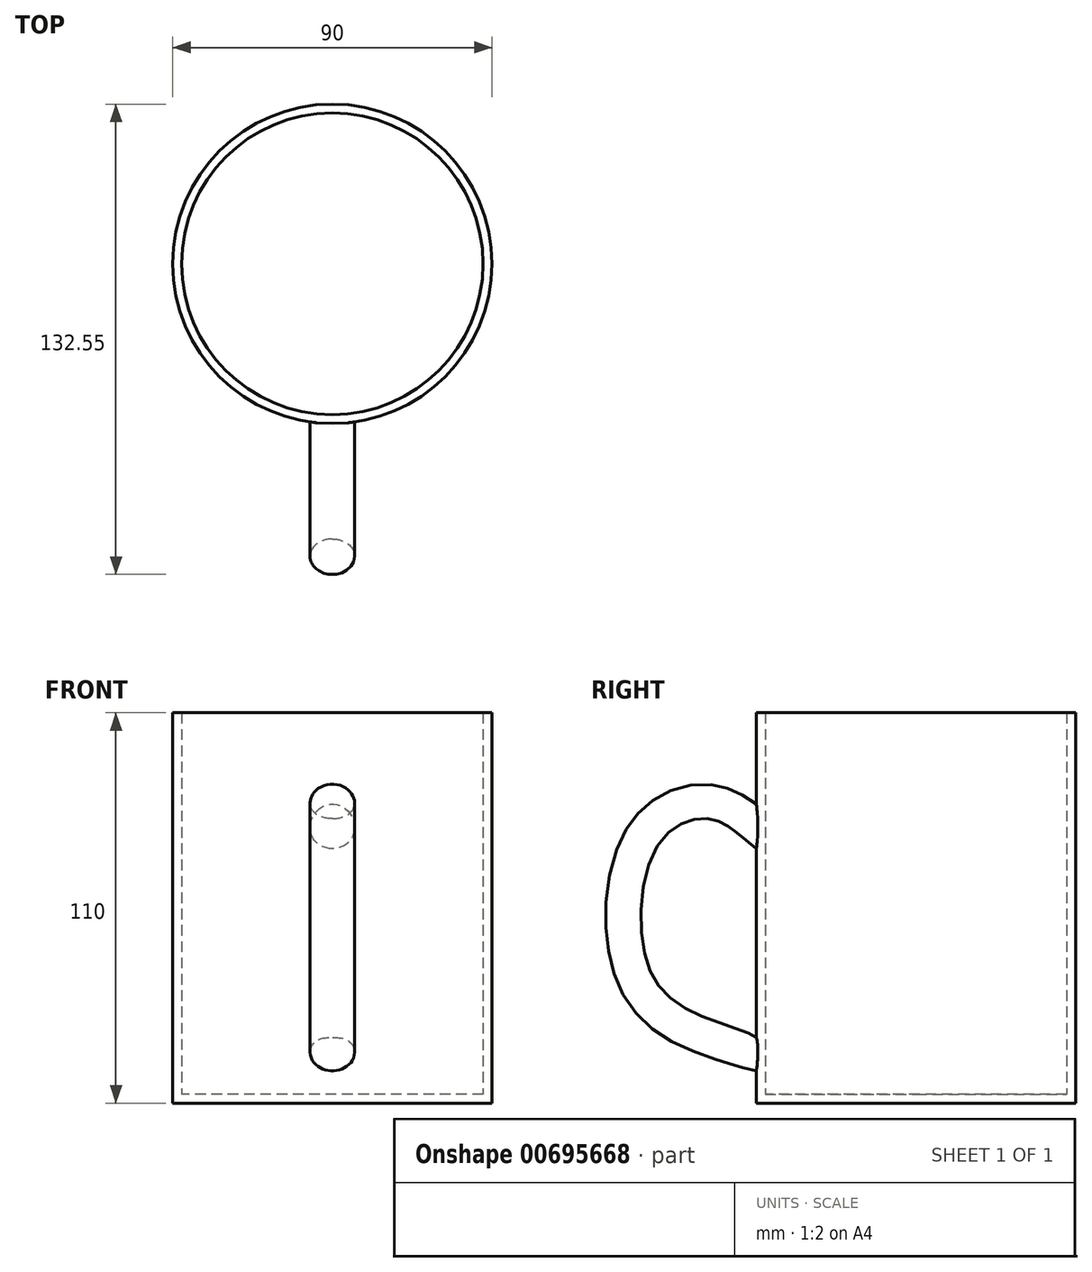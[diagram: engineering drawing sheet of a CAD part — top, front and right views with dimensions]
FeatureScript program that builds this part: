
annotation { "Feature Type Name" : "Feature", "Feature Type Description" : "" }
export const myFeature = defineFeature(function(context is Context, id is Id, definition is map)
    precondition{}
    {
        {
            var Q0;
            Q0=qCreatedBy(makeId("Top.planeOp"),FACE);
            var sketch = newSketch(context, id + "F0", { "sketchPlane" : qUnion([Q0])});
            skCircle(sketch, "E0", {"center": v(0, 0) * mm, "radius": 45 * mm});
            skSolve(sketch);
        }
        {
            var Q0;
            Q0=makeQuery(id+"F0.imprint","IMPRINT",FACE,{"disambiguationData":[TD([[makeQuery(id+"F0.imprint","IMPRINT",EDGE,{"derivedFrom":sQuery(id+"F0.wireOp",EDGE,"E0")}),1.0]])]});
            extrude(context, id + "F1", {"entities" : qUnion([Q0]), "depth" : 110 * mm, "offsetDistance" : 25 * mm});
        }
        {
            var Q0;
            Q0=qCreatedBy(makeId("Front.planeOp"),FACE);
            cPlane(context, id + "F2", {"entities" : qUnion([Q0]), "cplaneType" : CPlaneType.OFFSET, "offset" : 45 * mm, "width" : 150 * mm, "height" : 150 * mm});
        }
        {
            var Q0;
            Q0=qCreatedBy(id+"F2.planeOp",FACE);
            var sketch = newSketch(context, id + "F3", { "sketchPlane" : qUnion([Q0])});
            skCircle(sketch, "E1", {"center": v(0, 78) * mm, "radius": 6.28 * mm});
            skSolve(sketch);
        }
        {
            var Q0;
            Q0=qCreatedBy(makeId("Right.planeOp"),FACE);
            var sketch = newSketch(context, id + "F4", { "sketchPlane" : qUnion([Q0])});
            skFitSpline(sketch, "E2", {"points": [v(-44.41, 78.31) * mm, v(-58.33, 85.14) * mm, v(-77.58, 75.02) * mm, v(-78.46, 32.62) * mm, v(-53.14, 15.97) * mm, v(-37.13, 14.62) * mm], "startDerivative": vector(-78.07, 57.87) * mm, "endDerivative": vector(64.24, 44.63) * mm});
            skSolve(sketch);
        }
        {
            var Q0;
            Q0=makeQuery(id+"F3.imprint","IMPRINT",FACE,{"disambiguationData":[TD([[makeQuery(id+"F3.imprint","IMPRINT",EDGE,{"derivedFrom":sQuery(id+"F3.wireOp",EDGE,"E1")}),1.0]])]});
            var Q1;
            Q1=sQuery(id+"F4.wireOp",EDGE,"E2");
            sweep(context, id + "F5", {"operationType" : NewBodyOperationType.ADD, "profiles" : qUnion([Q0]), "path" : qUnion([Q1])});
        }
        {
            var Q0;
            Q0=makeQuery(id+"F1.opExtrude","CAP_FACE",FACE,{"disambiguationData":[OSD([sQuery(id+"F0.wireOp",EDGE,"E0")])],"isStart":false});
            shell(context, id + "F6", {"entities" : qUnion([Q0]), "thickness" : 2.5 * mm});
        }
    });
